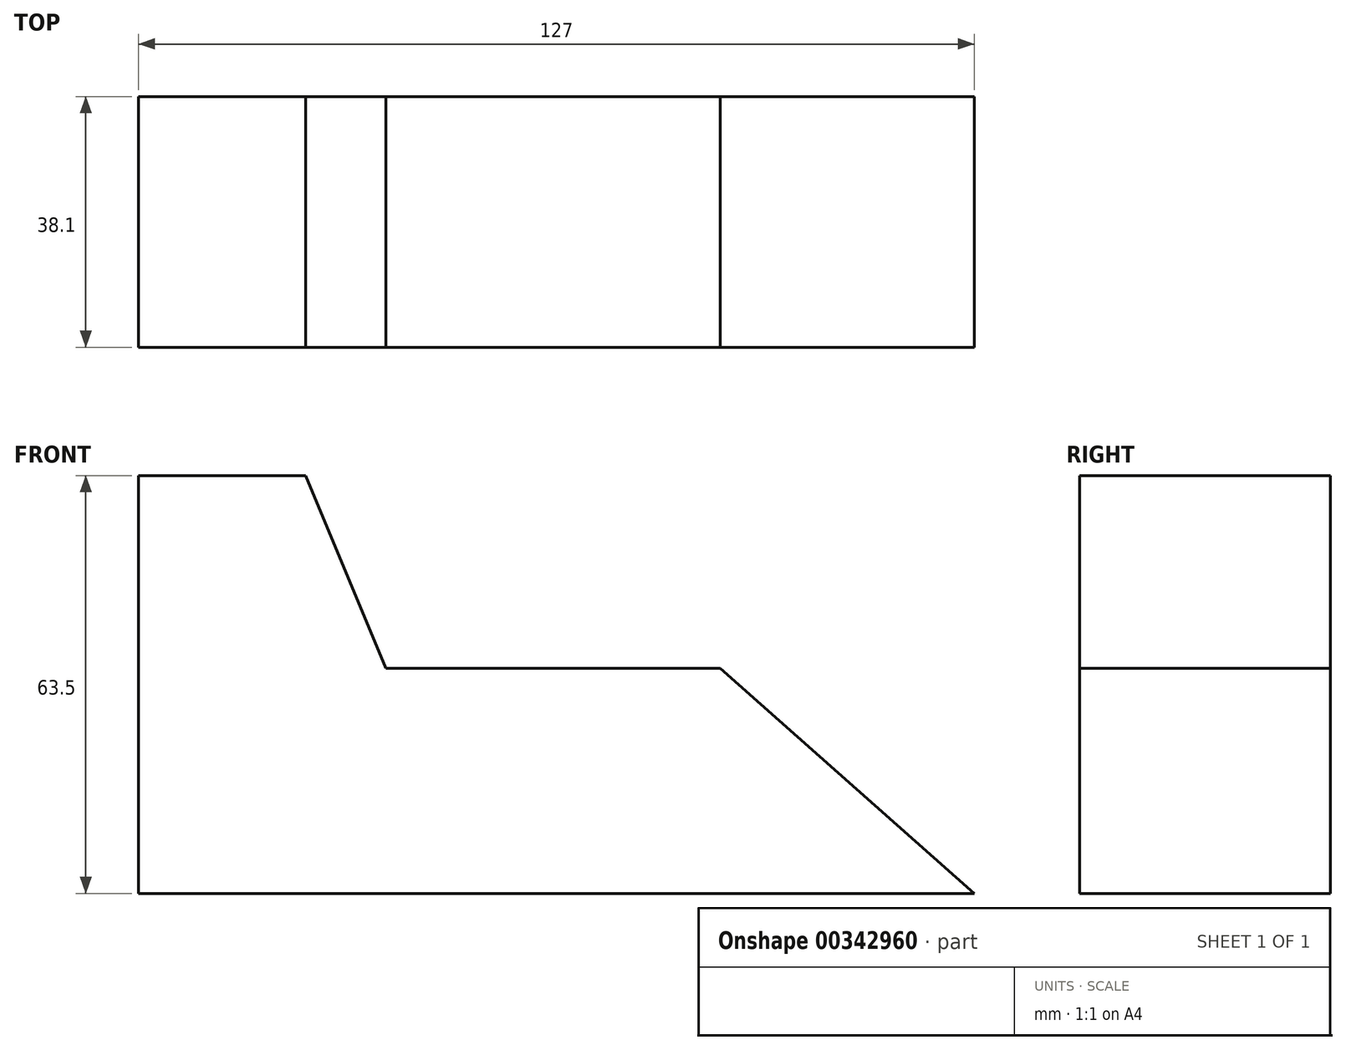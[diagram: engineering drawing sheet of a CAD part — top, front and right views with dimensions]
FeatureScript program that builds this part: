
annotation { "Feature Type Name" : "Feature", "Feature Type Description" : "" }
export const myFeature = defineFeature(function(context is Context, id is Id, definition is map)
    precondition{}
    {
        {
            var Q0;
            Q0=qCreatedBy(makeId("Front.planeOp"),FACE);
            var sketch = newSketch(context, id + "F0", { "sketchPlane" : qUnion([Q0])});
            skLineSegment(sketch, "E0", {"start": v(-65.67, -50.99) * mm, "end": v(61.33, -50.99) * mm});
            skLineSegment(sketch, "E1", {"start": v(-65.67, -50.99) * mm, "end": v(-65.67, 12.51) * mm});
            skLineSegment(sketch, "E2", {"start": v(-65.67, 12.51) * mm, "end": v(-40.27, 12.51) * mm});
            skLineSegment(sketch, "E3", {"start": v(-40.27, 12.51) * mm, "end": v(-28.1, -16.81) * mm});
            skLineSegment(sketch, "E4", {"start": v(-28.1, -16.81) * mm, "end": v(22.7, -16.81) * mm});
            skLineSegment(sketch, "E5", {"start": v(22.7, -16.81) * mm, "end": v(61.33, -50.99) * mm});
            skSolve(sketch);
        }
        {
            var Q0;
            Q0 = qSketchRegion(id + "F0", true);
            extrude(context, id + "F1", {"entities" : qUnion([Q0]), "depth" : 38.1 * mm});
        }
    });
